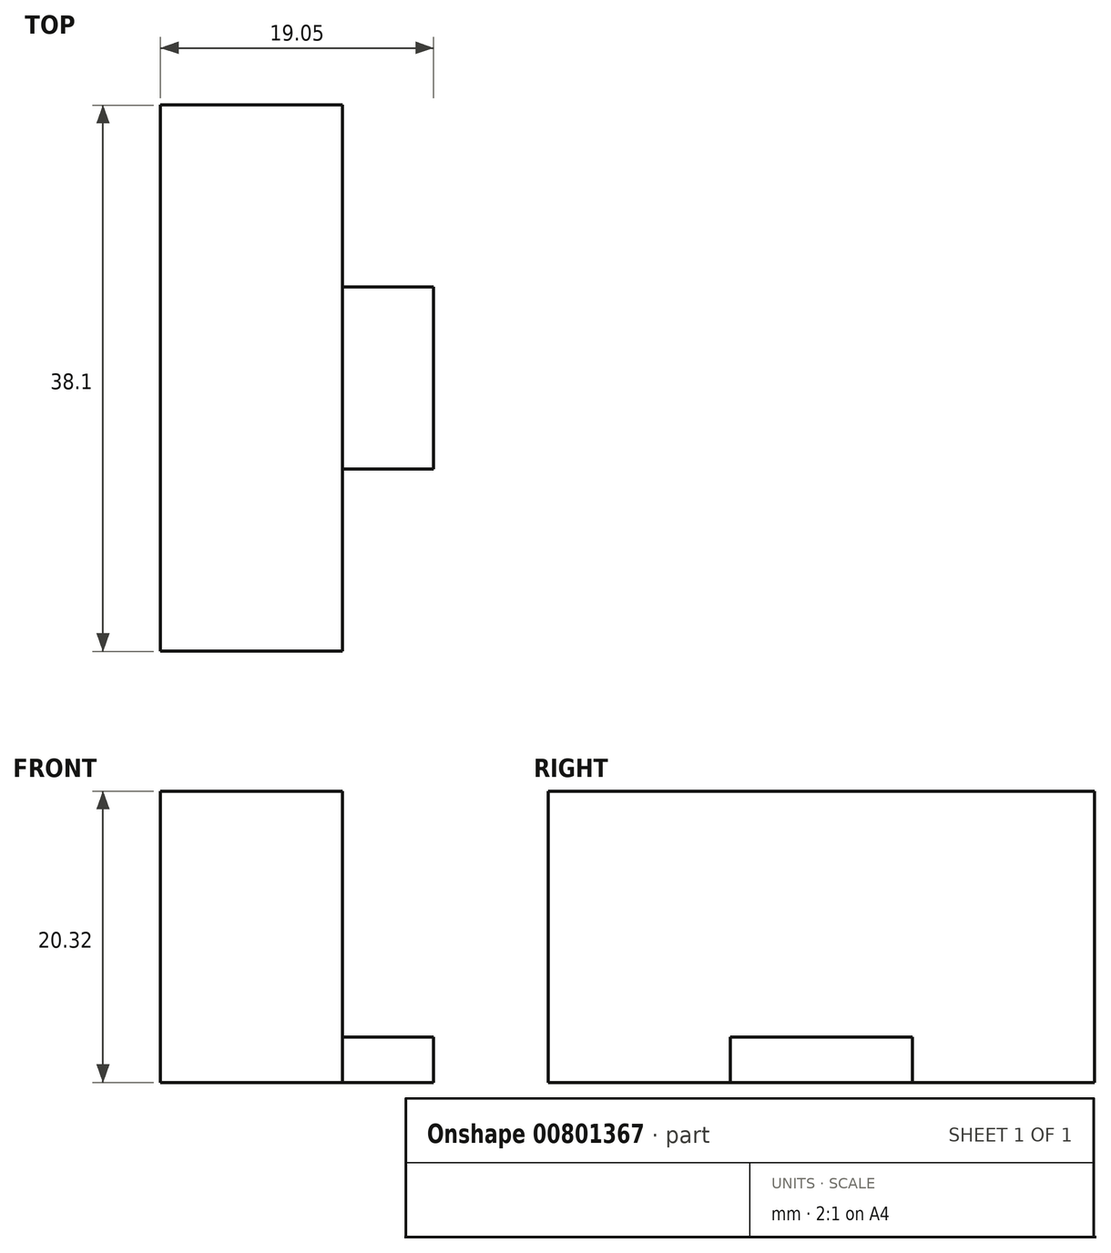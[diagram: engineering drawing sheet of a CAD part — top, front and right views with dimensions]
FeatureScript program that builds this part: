
annotation { "Feature Type Name" : "Feature", "Feature Type Description" : "" }
export const myFeature = defineFeature(function(context is Context, id is Id, definition is map)
    precondition{}
    {
        {
            var Q0;
            Q0=qCreatedBy(makeId("Top.planeOp"),FACE);
            var sketch = newSketch(context, id + "F0", { "sketchPlane" : qUnion([Q0])});
            skLineSegment(sketch, "E0.bottom", {"start": v(-38.68, -7.34) * mm, "end": v(-19.63, -7.34) * mm});
            skLineSegment(sketch, "E0.top", {"start": v(-38.68, 30.76) * mm, "end": v(-19.63, 30.76) * mm});
            skLineSegment(sketch, "E0.left", {"start": v(-38.68, -7.34) * mm, "end": v(-38.68, 30.76) * mm});
            skLineSegment(sketch, "E0.right", {"start": v(-19.63, -7.34) * mm, "end": v(-19.63, 30.76) * mm});
            skSolve(sketch);
        }
        {
            var Q0;
            Q0 = qSketchRegion(id + "F0", true);
            extrude(context, id + "F1", {"entities" : qUnion([Q0]), "depth" : 3.17 * mm, "offsetDistance" : 25.4 * mm});
        }
        {
            var Q0;
            Q0=makeQuery(id+"F1.opExtrude","CAP_FACE",FACE,{"disambiguationData":[OSD([sQuery(id+"F0.wireOp",EDGE,"E0.bottom"),sQuery(id+"F0.wireOp",EDGE,"E0.top"),sQuery(id+"F0.wireOp",EDGE,"E0.left"),sQuery(id+"F0.wireOp",EDGE,"E0.right")])],"isStart":false});
            var sketch = newSketch(context, id + "F2", { "sketchPlane" : qUnion([Q0])});
            skLineSegment(sketch, "E1.bottom", {"start": v(-25.98, -7.34) * mm, "end": v(-38.68, -7.34) * mm});
            skLineSegment(sketch, "E1.top", {"start": v(-25.98, 30.76) * mm, "end": v(-38.68, 30.76) * mm});
            skLineSegment(sketch, "E1.left", {"start": v(-25.98, -7.34) * mm, "end": v(-25.98, 30.76) * mm});
            skLineSegment(sketch, "E1.right", {"start": v(-38.68, -7.34) * mm, "end": v(-38.68, 30.76) * mm});
            skSolve(sketch);
        }
        {
            var Q0;
            Q0 = qSketchRegion(id + "F2", true);
            extrude(context, id + "F3", {"entities" : qUnion([Q0]), "operationType" : NewBodyOperationType.ADD, "depth" : 17.14 * mm, "offsetDistance" : 25.4 * mm});
        }
        {
            var Q0;
            Q0=makeQuery(id+"F1.opExtrude","CAP_FACE",FACE,{"disambiguationData":[OSD([sQuery(id+"F0.wireOp",EDGE,"E0.bottom"),sQuery(id+"F0.wireOp",EDGE,"E0.top"),sQuery(id+"F0.wireOp",EDGE,"E0.left"),sQuery(id+"F0.wireOp",EDGE,"E0.right")])],"isStart":false});
            var sketch = newSketch(context, id + "F4", { "sketchPlane" : qUnion([Q0])});
            skLineSegment(sketch, "E2.bottom", {"start": v(-19.63, -7.34) * mm, "end": v(-25.98, -7.34) * mm});
            skLineSegment(sketch, "E2.top", {"start": v(-19.63, 5.36) * mm, "end": v(-25.98, 5.36) * mm});
            skLineSegment(sketch, "E2.left", {"start": v(-19.63, -7.34) * mm, "end": v(-19.63, 5.36) * mm});
            skLineSegment(sketch, "E2.right", {"start": v(-25.98, -7.34) * mm, "end": v(-25.98, 5.36) * mm});
            skLineSegment(sketch, "E3.bottom", {"start": v(-19.63, 30.76) * mm, "end": v(-25.98, 30.76) * mm});
            skLineSegment(sketch, "E3.top", {"start": v(-19.63, 18.06) * mm, "end": v(-25.98, 18.06) * mm});
            skLineSegment(sketch, "E3.left", {"start": v(-19.63, 30.76) * mm, "end": v(-19.63, 18.06) * mm});
            skLineSegment(sketch, "E3.right", {"start": v(-25.98, 30.76) * mm, "end": v(-25.98, 18.06) * mm});
            skSolve(sketch);
        }
        {
            var Q0;
            Q0 = qSketchRegion(id + "F4", true);
            extrude(context, id + "F5", {"entities" : qUnion([Q0]), "operationType" : NewBodyOperationType.REMOVE, "oppositeDirection" : true, "depth" : 3.17 * mm, "offsetDistance" : 25.4 * mm});
        }
    });
